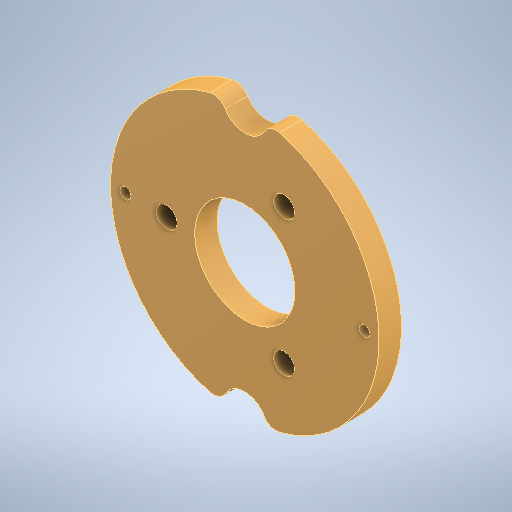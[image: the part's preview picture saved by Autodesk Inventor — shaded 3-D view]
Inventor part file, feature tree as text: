
AUTODESK INVENTOR PART (.ipt)
format: ipt  version: 2025.2 (Build 292293000, 293)  size: 317,440 bytes
history: native  units: in
note: dims shown in document units (in); Inventor stores cm internally (conversion verified against a paired STEP export)
features: extrude x3, sketch x3, other x2
ambient origin geometry x8: Origin, YZ Plane, XZ Plane, XY Plane, X Axis, Y Axis, Z Axis, Center Point
bodies: Solid1 (feature_tree), Solid2 (feature_tree)
feature tree (8):
  extrude  "Extrusion1"  Depth=0.1811in
  extrude  "Extrusion2"  Depth=0.1811in
  extrude  "Extrusion3"  Depth=0.3937in
  sketch  "Sketch1"  dims[d0=0.1811in d1=0.1811in]
  sketch  "Sketch2"  dims[d2=0.1811in d3=0.1811in]
  sketch  "Sketch3"  dims[d4=0.1811in d5=0.1811in d6=0.3937in d7=0.0in d8=0.1969in d9=0.0in d10=0.3937in d11=0.0in]
  other  "Com_SlipRing_stage"
  other  "SlipRing_stage (1)"
